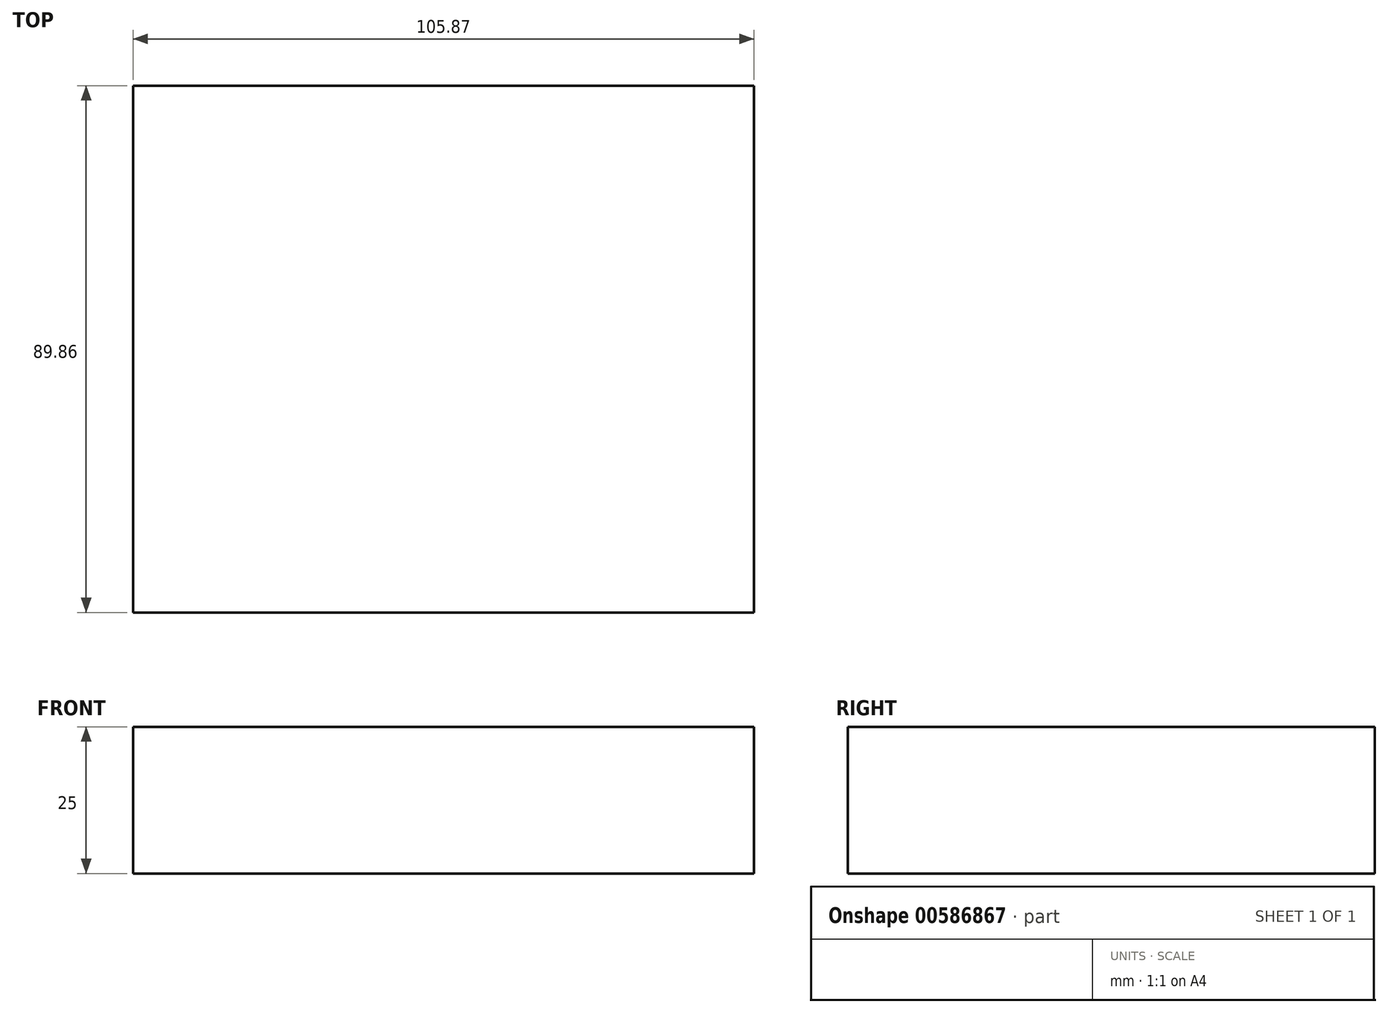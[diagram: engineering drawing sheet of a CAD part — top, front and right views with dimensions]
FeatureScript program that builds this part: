
annotation { "Feature Type Name" : "Feature", "Feature Type Description" : "" }
export const myFeature = defineFeature(function(context is Context, id is Id, definition is map)
    precondition{}
    {
        {
            var Q0;
            Q0=qCreatedBy(makeId("Top.planeOp"),FACE);
            var sketch = newSketch(context, id + "F0", { "sketchPlane" : qUnion([Q0])});
            skLineSegment(sketch, "E0.bottom", {"start": v(-49.45, 41.16) * mm, "end": v(56.42, 41.16) * mm});
            skLineSegment(sketch, "E0.top", {"start": v(-49.45, -48.7) * mm, "end": v(56.42, -48.7) * mm});
            skLineSegment(sketch, "E0.left", {"start": v(-49.45, 41.16) * mm, "end": v(-49.45, -48.7) * mm});
            skLineSegment(sketch, "E0.right", {"start": v(56.42, 41.16) * mm, "end": v(56.42, -48.7) * mm});
            skSolve(sketch);
        }
        {
            var Q0;
            Q0=makeQuery(id+"F0.imprint","IMPRINT",FACE,{"disambiguationData":[TD([[makeQuery(id+"F0.imprint","IMPRINT",EDGE,{"derivedFrom":sQuery(id+"F0.wireOp",EDGE,"E0.bottom")}),-1.0]])]});
            extrude(context, id + "F1", {"entities" : qUnion([Q0]), "depth" : 25 * mm, "offsetDistance" : 25 * mm});
        }
    });
